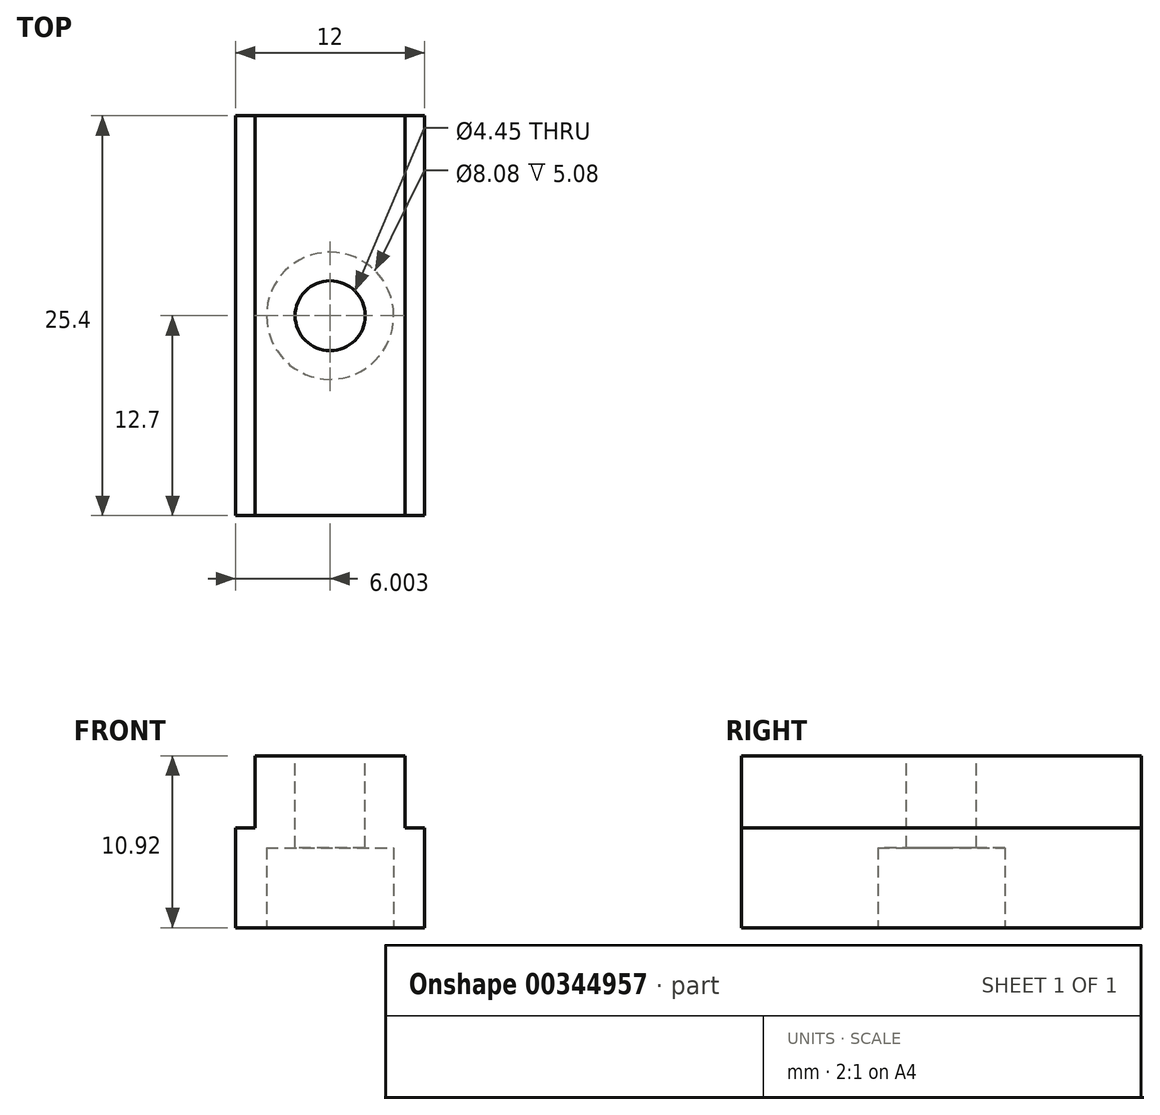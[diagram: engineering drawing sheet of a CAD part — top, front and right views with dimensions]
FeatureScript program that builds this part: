
annotation { "Feature Type Name" : "Feature", "Feature Type Description" : "" }
export const myFeature = defineFeature(function(context is Context, id is Id, definition is map)
    precondition{}
    {
        {
            var Q0;
            Q0=qCreatedBy(makeId("Front.planeOp"),FACE);
            var sketch = newSketch(context, id + "F0", { "sketchPlane" : qUnion([Q0])});
            skLineSegment(sketch, "E0.bottom", {"start": v(0, 4.57) * mm, "end": v(9.52, 4.57) * mm});
            skLineSegment(sketch, "E0.top", {"start": v(0, 0) * mm, "end": v(9.52, 0) * mm});
            skLineSegment(sketch, "E0.left", {"start": v(0, 4.57) * mm, "end": v(0, 0) * mm});
            skLineSegment(sketch, "E0.right", {"start": v(9.52, 4.57) * mm, "end": v(9.52, 0) * mm});
            skLineSegment(sketch, "E1.bottom", {"start": v(-1.24, -6.35) * mm, "end": v(10.76, -6.35) * mm});
            skLineSegment(sketch, "E1.top", {"start": v(-1.24, 0) * mm, "end": v(10.76, 0) * mm});
            skLineSegment(sketch, "E1.left", {"start": v(-1.24, -6.35) * mm, "end": v(-1.24, 0) * mm});
            skLineSegment(sketch, "E1.right", {"start": v(10.76, -6.35) * mm, "end": v(10.76, 0) * mm});
            skLineSegment(sketch, "E2", {"start": v(10.76, -3.18) * mm, "end": v(-1.24, -3.18) * mm, "construction": true});
            skLineSegment(sketch, "E3", {"start": v(4.76, 0) * mm, "end": v(4.76, -6.35) * mm, "construction": true});
            skLineSegment(sketch, "E4", {"start": v(4.76, 0) * mm, "end": v(4.76, 4.57) * mm, "construction": true});
            skSolve(sketch);
        }
        {
            var Q0;
            Q0=makeQuery(id+"F0.imprint","IMPRINT",FACE,{"disambiguationData":[TD([[makeQuery(id+"F0.imprint","IMPRINT",EDGE,{"derivedFrom":sQuery(id+"F0.wireOp",EDGE,"E0.bottom")}),-1.0]])]});
            var Q1;
            Q1=makeQuery(id+"F0.imprint","IMPRINT",FACE,{"disambiguationData":[TD([[makeQuery(id+"F0.imprint","IMPRINT",EDGE,{"derivedFrom":sQuery(id+"F0.wireOp",EDGE,"E1.bottom")}),1.0]])]});
            extrude(context, id + "F1", {"entities" : qUnion([Q0, Q1]), "depth" : 25.4 * mm});
        }
        {
            var Q0;
            Q0=makeQuery(id+"F1.opExtrude","SWEPT_FACE",FACE,{"disambiguationData":[OSD([sQuery(id+"F0.wireOp",EDGE,"E0.bottom")])]});
            var sketch = newSketch(context, id + "F2", { "sketchPlane" : qUnion([Q0])});
            skCircle(sketch, "E5", {"center": v(4.76, -12.7) * mm, "radius": 2.22 * mm});
            skSolve(sketch);
        }
        {
            var Q0;
            Q0=makeQuery(id+"F2.imprint","IMPRINT",FACE,{"disambiguationData":[TD([[makeQuery(id+"F2.imprint","IMPRINT",EDGE,{"derivedFrom":sQuery(id+"F2.wireOp",EDGE,"E5")}),1.0]])]});
            extrude(context, id + "F3", {"entities" : qUnion([Q0]), "operationType" : NewBodyOperationType.REMOVE, "endBound" : BoundingType.THROUGH_ALL, "oppositeDirection" : true, "depth" : 5.08 * mm});
        }
        {
            var Q0;
            Q0=makeQuery(id+"F1.opExtrude","SWEPT_FACE",FACE,{"disambiguationData":[OSD([sQuery(id+"F0.wireOp",EDGE,"E1.bottom")])]});
            var sketch = newSketch(context, id + "F4", { "sketchPlane" : qUnion([Q0])});
            skCircle(sketch, "E6", {"center": v(4.76, 12.7) * mm, "radius": 4.04 * mm});
            skSolve(sketch);
        }
        {
            var Q0;
            Q0=makeQuery(id+"F4.imprint","IMPRINT",FACE,{"disambiguationData":[TD([[makeQuery(id+"F4.imprint","IMPRINT",EDGE,{"derivedFrom":sQuery(id+"F4.wireOp",EDGE,"E6")}),1.0]])]});
            extrude(context, id + "F5", {"entities" : qUnion([Q0]), "operationType" : NewBodyOperationType.REMOVE, "oppositeDirection" : true, "depth" : 5.08 * mm});
        }
    });
